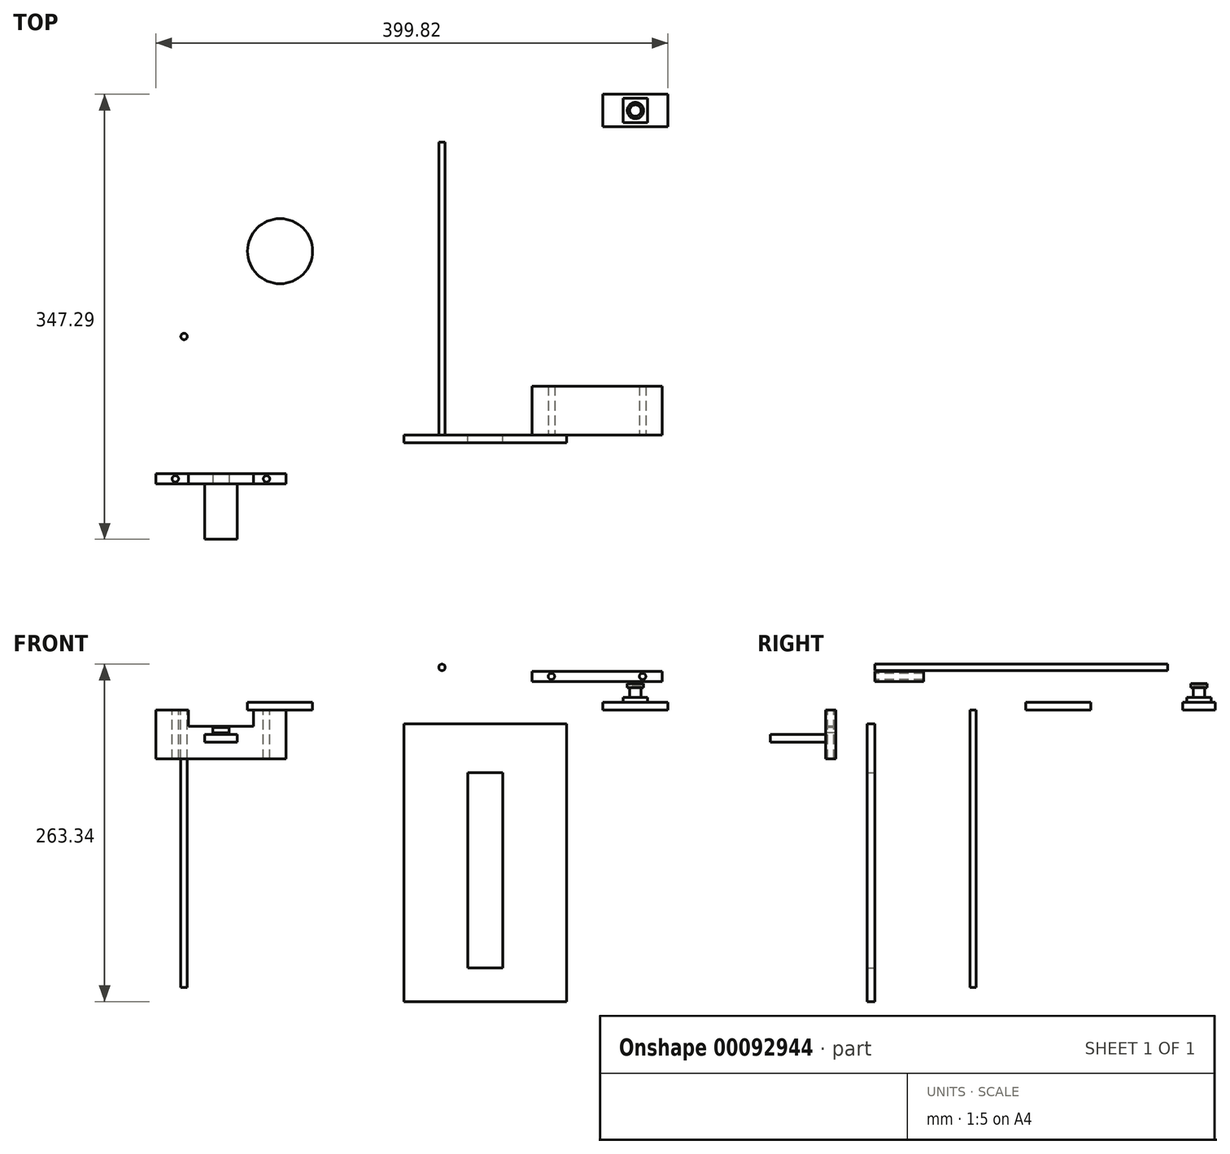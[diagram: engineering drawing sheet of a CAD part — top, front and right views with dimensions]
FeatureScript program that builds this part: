
annotation { "Feature Type Name" : "Feature", "Feature Type Description" : "" }
export const myFeature = defineFeature(function(context is Context, id is Id, definition is map)
    precondition{}
    {
        {
            var Q0;
            Q0=qCreatedBy(makeId("Front.planeOp"),FACE);
            var sketch = newSketch(context, id + "F0", { "sketchPlane" : qUnion([Q0])});
            skLineSegment(sketch, "E0.bottom", {"start": v(110.99, 22.28) * mm, "end": v(9.39, 22.28) * mm});
            skLineSegment(sketch, "E0.top", {"start": v(110.99, 30.28) * mm, "end": v(9.39, 30.28) * mm});
            skLineSegment(sketch, "E0.left", {"start": v(110.99, 22.28) * mm, "end": v(110.99, 30.28) * mm});
            skLineSegment(sketch, "E0.right", {"start": v(9.39, 22.28) * mm, "end": v(9.39, 30.28) * mm});
            skPoint(sketch, "E0.middle", {"position": v(60.19, 26.28) * mm});
            skCircle(sketch, "E1", {"center": v(24.59, 26.28) * mm, "radius": 2.5 * mm});
            skCircle(sketch, "E2", {"center": v(95.79, 26.28) * mm, "radius": 2.5 * mm});
            skSolve(sketch);
        }
        {
            var Q0;
            Q0=qCreatedBy(makeId("Front.planeOp"),FACE);
            var sketch = newSketch(context, id + "F1", { "sketchPlane" : qUnion([Q0])});
            skCircle(sketch, "E3", {"center": v(-60.87, 33.38) * mm, "radius": 2.5 * mm});
            skSolve(sketch);
        }
        {
            var Q0;
            Q0 = qSketchRegion(id + "F1", true);
            extrude(context, id + "F2", {"entities" : qUnion([Q0]), "oppositeDirection" : true, "depth" : 228.6 * mm});
        }
        {
            var Q0;
            Q0 = qSketchRegion(id + "F0", true);
            extrude(context, id + "F3", {"entities" : qUnion([Q0]), "oppositeDirection" : true, "depth" : 38.1 * mm});
        }
        {
            var Q0;
            Q0=qCreatedBy(makeId("Top.planeOp"),FACE);
            var sketch = newSketch(context, id + "F4", { "sketchPlane" : qUnion([Q0])});
            skLineSegment(sketch, "E4.bottom", {"start": v(-182.67, -38.3) * mm, "end": v(-284.27, -38.3) * mm});
            skLineSegment(sketch, "E4.top", {"start": v(-182.67, -30.3) * mm, "end": v(-284.27, -30.3) * mm});
            skLineSegment(sketch, "E4.left", {"start": v(-182.67, -38.3) * mm, "end": v(-182.67, -30.3) * mm});
            skLineSegment(sketch, "E4.right", {"start": v(-284.27, -38.3) * mm, "end": v(-284.27, -30.3) * mm});
            skPoint(sketch, "E4.middle", {"position": v(-233.47, -34.3) * mm});
            skCircle(sketch, "E5", {"center": v(-197.87, -34.3) * mm, "radius": 2.5 * mm});
            skCircle(sketch, "E6", {"center": v(-269.07, -34.3) * mm, "radius": 2.5 * mm});
            skSolve(sketch);
        }
        {
            var Q0;
            Q0 = qSketchRegion(id + "F4", true);
            extrude(context, id + "F5", {"entities" : qUnion([Q0]), "oppositeDirection" : true, "depth" : 38.1 * mm});
        }
        {
            var Q0;
            Q0=qCreatedBy(makeId("Top.planeOp"),FACE);
            var sketch = newSketch(context, id + "F6", { "sketchPlane" : qUnion([Q0])});
            skCircle(sketch, "E7", {"center": v(-262.25, 76.84) * mm, "radius": 2.5 * mm});
            skSolve(sketch);
        }
        {
            var Q0;
            Q0 = qSketchRegion(id + "F6", true);
            extrude(context, id + "F7", {"entities" : qUnion([Q0]), "oppositeDirection" : true, "depth" : 216.61 * mm});
        }
        {
            var Q0;
            Q0=qCreatedBy(makeId("Front.planeOp"),FACE);
            var sketch = newSketch(context, id + "F8", { "sketchPlane" : qUnion([Q0])});
            skLineSegment(sketch, "E8.bottom", {"start": v(36.41, -227.46) * mm, "end": v(-90.59, -227.46) * mm});
            skLineSegment(sketch, "E8.top", {"start": v(36.41, -10.84) * mm, "end": v(-90.59, -10.84) * mm});
            skLineSegment(sketch, "E8.left", {"start": v(36.41, -227.46) * mm, "end": v(36.41, -10.84) * mm});
            skLineSegment(sketch, "E8.right", {"start": v(-90.59, -227.46) * mm, "end": v(-90.59, -10.84) * mm});
            skPoint(sketch, "E8.middle", {"position": v(-27.09, -119.15) * mm});
            skLineSegment(sketch, "E9.bottom", {"start": v(-13.39, -201.34) * mm, "end": v(-40.79, -201.34) * mm});
            skLineSegment(sketch, "E9.top", {"start": v(-13.39, -48.94) * mm, "end": v(-40.79, -48.94) * mm});
            skLineSegment(sketch, "E9.left", {"start": v(-13.39, -201.34) * mm, "end": v(-13.39, -48.94) * mm});
            skLineSegment(sketch, "E9.right", {"start": v(-40.79, -201.34) * mm, "end": v(-40.79, -48.94) * mm});
            skPoint(sketch, "E9.middle", {"position": v(-27.09, -125.14) * mm});
            skSolve(sketch);
        }
        {
            var Q0;
            Q0 = qSketchRegion(id + "F8", true);
            extrude(context, id + "F9", {"entities" : qUnion([Q0]), "depth" : 6 * mm});
        }
        {
            var Q0;
            Q0=qCreatedBy(makeId("Top.planeOp"),FACE);
            var sketch = newSketch(context, id + "F10", { "sketchPlane" : qUnion([Q0])});
            skCircle(sketch, "E10", {"center": v(-187.3, 143.4) * mm, "radius": 25.4 * mm});
            skSolve(sketch);
        }
        {
            var Q0;
            Q0 = qSketchRegion(id + "F10", true);
            extrude(context, id + "F11", {"entities" : qUnion([Q0]), "depth" : 6 * mm});
        }
        {
            var Q0;
            Q0=qCreatedBy(makeId("Top.planeOp"),FACE);
            var sketch = newSketch(context, id + "F12", { "sketchPlane" : qUnion([Q0])});
            skLineSegment(sketch, "E11.bottom", {"start": v(115.55, 240.5) * mm, "end": v(64.75, 240.5) * mm});
            skLineSegment(sketch, "E11.top", {"start": v(115.55, 265.9) * mm, "end": v(64.75, 265.9) * mm});
            skLineSegment(sketch, "E11.left", {"start": v(115.55, 240.5) * mm, "end": v(115.55, 265.9) * mm});
            skLineSegment(sketch, "E11.right", {"start": v(64.75, 240.5) * mm, "end": v(64.75, 265.9) * mm});
            skPoint(sketch, "E11.middle", {"position": v(90.15, 253.2) * mm});
            skCircle(sketch, "E12", {"center": v(90.15, 253.2) * mm, "radius": 4.45 * mm});
            skLineSegment(sketch, "E13.bottom", {"start": v(99.68, 243.67) * mm, "end": v(80.63, 243.67) * mm});
            skLineSegment(sketch, "E13.top", {"start": v(99.68, 262.72) * mm, "end": v(80.63, 262.72) * mm});
            skLineSegment(sketch, "E13.left", {"start": v(99.68, 243.67) * mm, "end": v(99.68, 262.72) * mm});
            skLineSegment(sketch, "E13.right", {"start": v(80.63, 243.67) * mm, "end": v(80.63, 262.72) * mm});
            skSolve(sketch);
        }
        {
            var Q0;
            Q0=makeQuery(id+"F12.imprint","IMPRINT",FACE,{"disambiguationData":[TD([[makeQuery(id+"F12.imprint","IMPRINT",EDGE,{"derivedFrom":sQuery(id+"F12.wireOp",EDGE,"E11.bottom")}),-1.0]])]});
            var Q1;
            Q1=makeQuery(id+"F12.imprint","IMPRINT",FACE,{"disambiguationData":[TD([[makeQuery(id+"F12.imprint","IMPRINT",EDGE,{"derivedFrom":sQuery(id+"F12.wireOp",EDGE,"E12")}),-1.0]])]});
            var Q2;
            Q2=makeQuery(id+"F12.imprint","IMPRINT",FACE,{"disambiguationData":[TD([[makeQuery(id+"F12.imprint","IMPRINT",EDGE,{"derivedFrom":sQuery(id+"F12.wireOp",EDGE,"E12")}),1.0]])]});
            extrude(context, id + "F13", {"entities" : qUnion([Q0, Q1, Q2]), "depth" : 6 * mm});
        }
        {
            var Q0;
            Q0=makeQuery(id+"F12.imprint","IMPRINT",FACE,{"disambiguationData":[TD([[makeQuery(id+"F12.imprint","IMPRINT",EDGE,{"derivedFrom":sQuery(id+"F12.wireOp",EDGE,"E12")}),-1.0]])]});
            extrude(context, id + "F14", {"entities" : qUnion([Q0]), "operationType" : NewBodyOperationType.ADD, "depth" : 10 * mm});
        }
        {
            var Q0;
            Q0=makeQuery(id+"F12.imprint","IMPRINT",FACE,{"disambiguationData":[TD([[makeQuery(id+"F12.imprint","IMPRINT",EDGE,{"derivedFrom":sQuery(id+"F12.wireOp",EDGE,"E12")}),1.0]])]});
            extrude(context, id + "F15", {"entities" : qUnion([Q0]), "operationType" : NewBodyOperationType.ADD, "depth" : 19.05 * mm});
        }
        {
            var Q0;
            Q0=makeQuery(id+"F15.opExtrude","CAP_FACE",FACE,{"disambiguationData":[OSD([sQuery(id+"F12.wireOp",EDGE,"E12")])],"isStart":false});
            var sketch = newSketch(context, id + "F16", { "sketchPlane" : qUnion([Q0])});
            skCircle(sketch, "E14", {"center": v(90.15, 253.2) * mm, "radius": 6.35 * mm});
            skCircle(sketch, "E15", {"center": v(90.15, 253.2) * mm, "radius": 4.45 * mm});
            skSolve(sketch);
        }
        {
            var Q0;
            Q0 = qSketchRegion(id + "F16", true);
            extrude(context, id + "F17", {"entities" : qUnion([Q0]), "operationType" : NewBodyOperationType.ADD, "endBound" : BoundingType.SYMMETRIC, "depth" : 3 * mm});
        }
        {
            var Q0;
            Q0=makeQuery(id+"F5.opExtrude","SWEPT_FACE",FACE,{"disambiguationData":[OSD([sQuery(id+"F4.wireOp",EDGE,"E4.bottom")])]});
            var sketch = newSketch(context, id + "F18", { "sketchPlane" : qUnion([Q0])});
            skLineSegment(sketch, "E16", {"start": v(-233.47, 0) * mm, "end": v(-233.47, -38.1) * mm, "construction": true});
            skLineSegment(sketch, "E17.bottom", {"start": v(-208.07, -19.05) * mm, "end": v(-258.87, -19.05) * mm});
            skLineSegment(sketch, "E17.top", {"start": v(-208.07, 0) * mm, "end": v(-258.87, 0) * mm});
            skLineSegment(sketch, "E17.left", {"start": v(-208.07, -19.05) * mm, "end": v(-208.07, 0) * mm});
            skLineSegment(sketch, "E17.right", {"start": v(-258.87, -19.05) * mm, "end": v(-258.87, 0) * mm});
            skPoint(sketch, "E17.middle", {"position": v(-233.47, -9.52) * mm});
            skLineSegment(sketch, "E18.bottom", {"start": v(-220.77, -25.05) * mm, "end": v(-246.17, -25.05) * mm});
            skLineSegment(sketch, "E18.top", {"start": v(-220.77, -19.05) * mm, "end": v(-246.17, -19.05) * mm});
            skLineSegment(sketch, "E18.left", {"start": v(-220.77, -25.05) * mm, "end": v(-220.77, -19.05) * mm});
            skLineSegment(sketch, "E18.right", {"start": v(-246.17, -25.05) * mm, "end": v(-246.17, -19.05) * mm});
            skPoint(sketch, "E18.middle", {"position": v(-233.47, -22.05) * mm});
            skLineSegment(sketch, "E19", {"start": v(-258.87, -12.7) * mm, "end": v(-208.07, -12.7) * mm});
            skPoint(sketch, "E19.endSnap0", {"position": v(-208.07, -9.52) * mm});
            skLineSegment(sketch, "E20.bottom", {"start": v(-233.47, -15.74) * mm, "end": v(-233.47, -15.74) * mm});
            skLineSegment(sketch, "E20.top", {"start": v(-233.47, -15.74) * mm, "end": v(-233.47, -15.74) * mm});
            skLineSegment(sketch, "E20.left", {"start": v(-233.47, -15.74) * mm, "end": v(-233.47, -15.74) * mm});
            skLineSegment(sketch, "E20.right", {"start": v(-233.47, -15.74) * mm, "end": v(-233.47, -15.74) * mm});
            skPoint(sketch, "E20.middle", {"position": v(-233.47, -15.74) * mm});
            skLineSegment(sketch, "E21.bottom", {"start": v(-227.12, -17.74) * mm, "end": v(-239.82, -17.74) * mm});
            skLineSegment(sketch, "E21.top", {"start": v(-227.12, -13.74) * mm, "end": v(-239.82, -13.74) * mm});
            skLineSegment(sketch, "E21.left", {"start": v(-227.12, -17.74) * mm, "end": v(-227.12, -13.74) * mm});
            skLineSegment(sketch, "E21.right", {"start": v(-239.82, -17.74) * mm, "end": v(-239.82, -13.74) * mm});
            skSolve(sketch);
        }
        {
            var Q0;
            Q0=makeQuery(id+"F18.imprint","IMPRINT",FACE,{"disambiguationData":[TD([[makeQuery(id+"F18.imprint","IMPRINT",EDGE,{"derivedFrom":sQuery(id+"F18.wireOp",EDGE,"E17.top")}),1.0]])]});
            var Q1;
            Q1=makeQuery(id+"F18.imprint","IMPRINT",FACE,{"disambiguationData":[TD([[makeQuery(id+"F18.imprint","IMPRINT",EDGE,{"derivedFrom":sQuery(id+"F18.wireOp",EDGE,"E21.bottom")}),-1.0]])]});
            extrude(context, id + "F19", {"entities" : qUnion([Q0, Q1]), "operationType" : NewBodyOperationType.REMOVE, "oppositeDirection" : true, "depth" : 8 * mm});
        }
        {
            var Q0;
            Q0=makeQuery(id+"F18.imprint","IMPRINT",FACE,{"disambiguationData":[TD([[makeQuery(id+"F18.imprint","IMPRINT",EDGE,{"derivedFrom":sQuery(id+"F18.wireOp",EDGE,"E18.bottom")}),-1.0]])]});
            extrude(context, id + "F20", {"entities" : qUnion([Q0]), "operationType" : NewBodyOperationType.ADD, "depth" : 38.1 * mm + 5 * mm});
        }
    });
